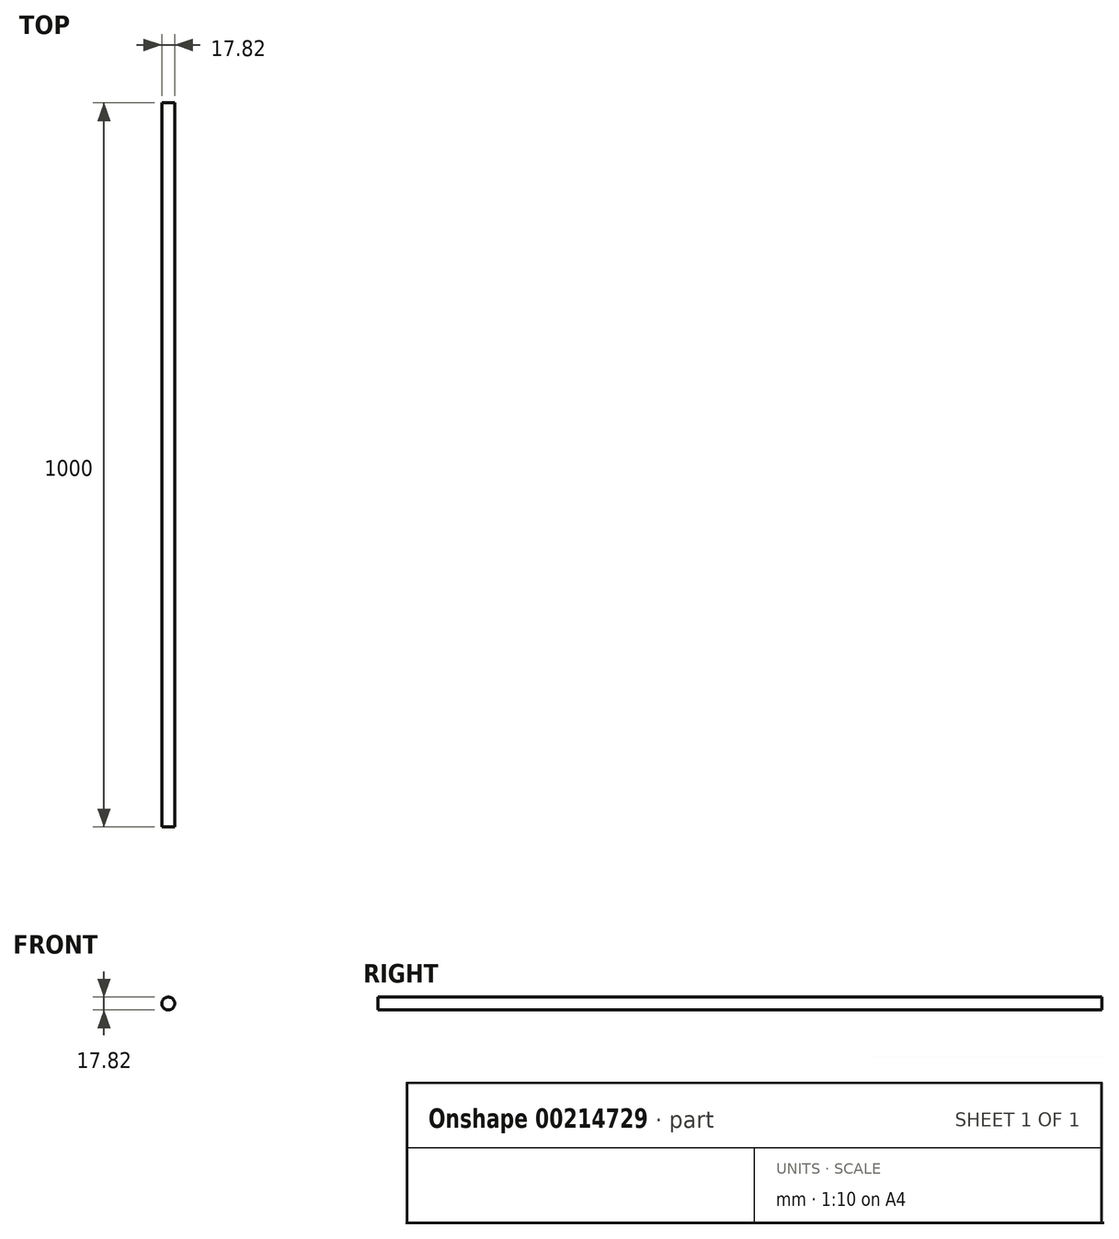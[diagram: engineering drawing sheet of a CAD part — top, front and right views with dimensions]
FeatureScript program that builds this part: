
annotation { "Feature Type Name" : "Feature", "Feature Type Description" : "" }
export const myFeature = defineFeature(function(context is Context, id is Id, definition is map)
    precondition{}
    {
        {
            var Q0;
            Q0=qCreatedBy(makeId("Front.planeOp"),FACE);
            var sketch = newSketch(context, id + "F0", { "sketchPlane" : qUnion([Q0])});
            skCircle(sketch, "E0", {"center": v(0, 0) * mm, "radius": 8.9 * mm});
            skSolve(sketch);
        }
        {
            var Q0;
            Q0=makeQuery(id+"F0.imprint","IMPRINT",FACE,{"disambiguationData":[TD([[makeQuery(id+"F0.imprint","IMPRINT",EDGE,{"derivedFrom":sQuery(id+"F0.wireOp",EDGE,"E0")}),1.0]])]});
            extrude(context, id + "F1", {"entities" : qUnion([Q0]), "depth" : 1000 * mm});
        }
    });
